# Revit family: BE21
name_source: partatom
category: Lighting Fixtures
revit_build: Autodesk Revit 2013 (Build: 20130531_2115(x64)
units: mm (PartAtom-declared; Revit-internal decimal feet)

## types (1)
- Era-BE21
    Apparent Load = 0 VA
    Arm Material = Metal-Kim Lighting-Aluminum Alloy
    Arm Visible = Yes
    Assembly Code = D5020200
    Color Filter = 16777215
    Description = Site/Roadway Luminaire
    Dimming Lamp Color Temperature Shift = <None>
    Emit Shape Visible in Rendering = No
    Emit from Circle Diameter = 16"
    Finish = All colors shall be a Super TGIC powder coat paint. Optional white (WH) and custom colors available.
    Glass Material = Glass-Kim Lighting-Clear
    Housing Material = Metal-Kim Lighting-Aluminum Alloy
    Inside Material = <By Category>
    Lamp = LED
    Load Classification = Lighting
    Manufacturer = Kim Lighting
    Manufacturer Fax = 626-369-2695
    MasterFormat Number = 26 56 16, 26 56 19, 26 56 29
    MasterFormat Title = Parking Lighting, Roadway Lighting, Site Lighting
    Model = Era Bell
    Mount Height = 192"
    Note Text = LF
    Note Visible = Yes
    Number of Poles = 1
    OmniClass Number = 23-80 70 14 21
    OmniClass Title = Street and Roadway Lighting
    Photometric Notes = More IES files download on Photometric Web Link
    Photometric Web File = be214e35-120l4k-nfo.ies
    Photometric Web Link = http://www.kimlighting.com
    Pole Finish = Metal-Kim Lighting-Aluminum Alloy
    Pole Height = 175 1/2"
    Power Factor = 1
    Product Documentation Link = https://hubbellcdn.com
    Product Page URL = http://www.kimlighting.com
    Revision Date = 11/29/2017
    Series = ERA Bell LUMINAIRE
    Tilt Angle = 90.00°
    Type Comments = Lighting Fixture
    URL = www.kimlighting.com/
    Voltage = 208 V
    Wattage Comments = 60 LEDs

## geometry (parser evidence)
native form markers: Blend x2, Sweep x7
no freeform markers — native parametric forms only
